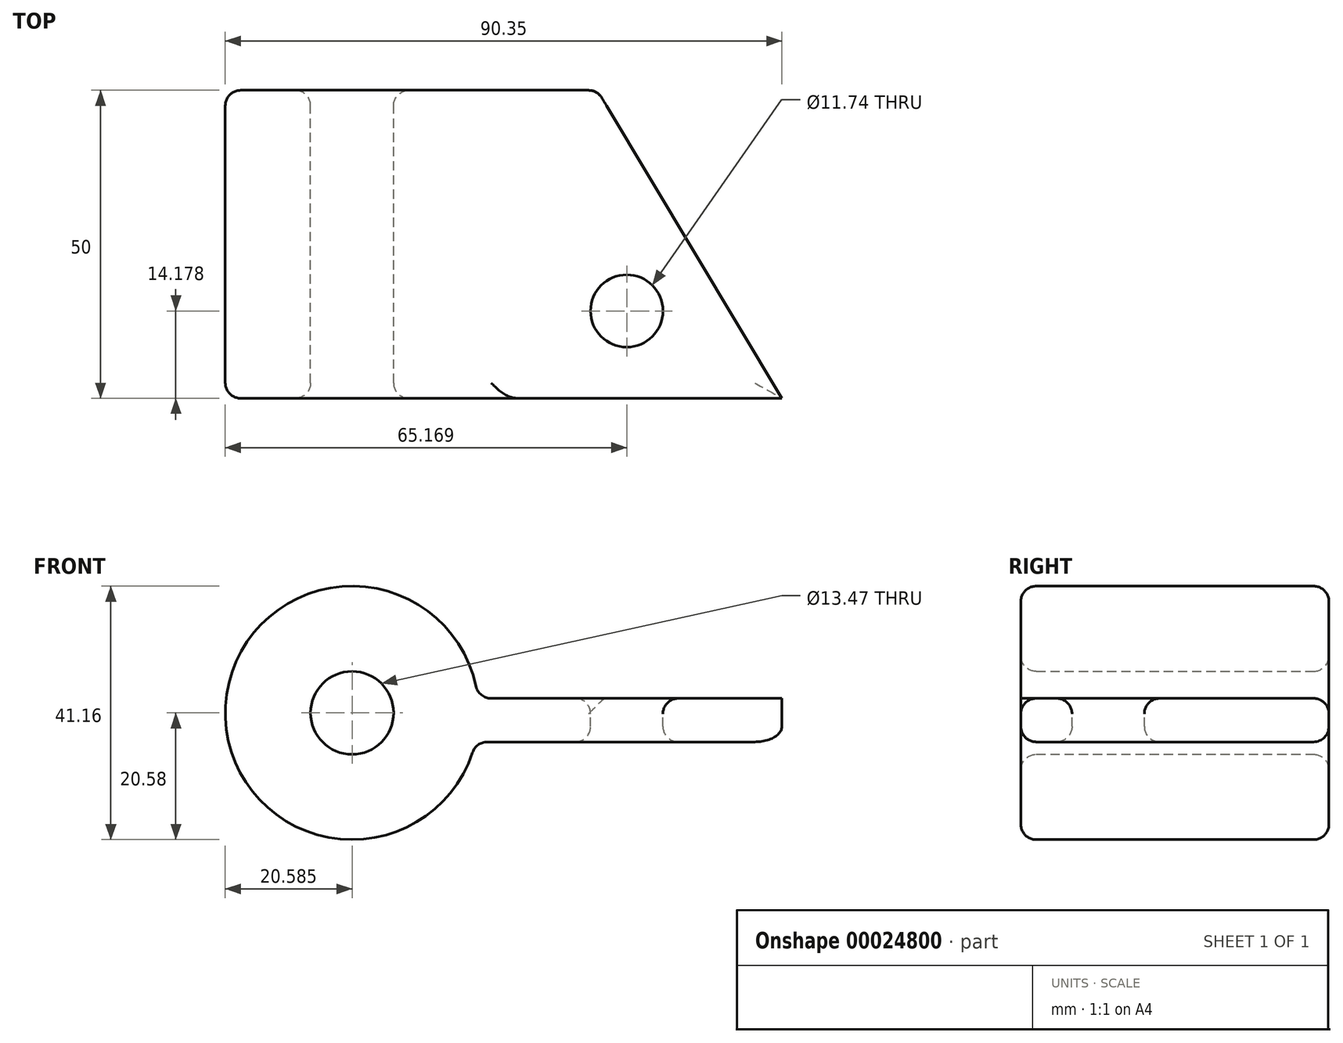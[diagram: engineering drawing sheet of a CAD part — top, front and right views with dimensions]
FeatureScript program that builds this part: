
annotation { "Feature Type Name" : "Feature", "Feature Type Description" : "" }
export const myFeature = defineFeature(function(context is Context, id is Id, definition is map)
    precondition{}
    {
        {
            var Q0;
            Q0=qCreatedBy(makeId("Front.planeOp"),FACE);
            var sketch = newSketch(context, id + "F0", { "sketchPlane" : qUnion([Q0])});
            skCircle(sketch, "E0", {"center": v(-44.76, 6.82) * mm, "radius": 20.58 * mm});
            skCircle(sketch, "E1", {"center": v(-44.76, 6.82) * mm, "radius": 6.74 * mm});
            skSolve(sketch);
        }
        {
            var Q0;
            Q0=makeQuery(id+"F0.imprint","IMPRINT",FACE,{"disambiguationData":[TD([[makeQuery(id+"F0.imprint","IMPRINT",EDGE,{"derivedFrom":sQuery(id+"F0.wireOp",EDGE,"E0")}),1.0]])]});
            extrude(context, id + "F1", {"entities" : qUnion([Q0]), "depth" : 50 * mm});
        }
        {
            var Q0;
            Q0=qCreatedBy(makeId("Right.planeOp"),FACE);
            var sketch = newSketch(context, id + "F2", { "sketchPlane" : qUnion([Q0])});
            skLineSegment(sketch, "E2.bottom", {"start": v(-50.14, 9.18) * mm, "end": v(0, 9.18) * mm});
            skLineSegment(sketch, "E2.top", {"start": v(-50.14, 2.1) * mm, "end": v(0, 2.1) * mm});
            skLineSegment(sketch, "E2.left", {"start": v(-50.14, 9.18) * mm, "end": v(-50.14, 2.1) * mm});
            skLineSegment(sketch, "E2.right", {"start": v(0, 9.18) * mm, "end": v(0, 2.1) * mm});
            skSolve(sketch);
        }
        {
            var Q0;
            Q0=makeQuery(id+"F2.imprint","IMPRINT",FACE,{"disambiguationData":[TD([[makeQuery(id+"F2.imprint","IMPRINT",EDGE,{"derivedFrom":sQuery(id+"F2.wireOp",EDGE,"E2.bottom")}),-1.0]])]});
            extrude(context, id + "F3", {"entities" : qUnion([Q0]), "oppositeDirection" : true, "depth" : 25 * mm});
        }
        {
            var Q0;
            Q0=makeQuery(id+"F3.opExtrude","SWEPT_BODY",BODY,{"disambiguationData":[OSD([sQuery(id+"F2.wireOp",EDGE,"E2.bottom"),sQuery(id+"F2.wireOp",EDGE,"E2.top"),sQuery(id+"F2.wireOp",EDGE,"E2.left"),sQuery(id+"F2.wireOp",EDGE,"E2.right")])]});
            var Q1;
            Q1=makeQuery(id+"F1.opExtrude","SWEPT_BODY",BODY,{"disambiguationData":[OSD([sQuery(id+"F0.wireOp",EDGE,"E0"),sQuery(id+"F0.wireOp",EDGE,"E1")])]});
            booleanBodies(context, id + "F4", {"operationType" : BooleanOperationType.UNION, "tools" : qUnion([Q0, Q1])});
        }
        {
            var Q0;
            Q0=makeQuery(id+"F3.opExtrude","CAP_FACE",FACE,{"disambiguationData":[OSD([sQuery(id+"F2.wireOp",EDGE,"E2.bottom"),sQuery(id+"F2.wireOp",EDGE,"E2.top"),sQuery(id+"F2.wireOp",EDGE,"E2.left"),sQuery(id+"F2.wireOp",EDGE,"E2.right")])],"isStart":true});
            extrude(context, id + "F5", {"entities" : qUnion([Q0]), "operationType" : NewBodyOperationType.ADD, "depth" : 25 * mm});
        }
        {
            var Q0;
            {var subQ0=sQuery(id+"F2.wireOp",EDGE,"E2.left");Q0=makeQuery(id+"F5.boolean.opBoolean","MERGE",FACE,{"derivedFrom":[makeQuery(id+"F3.opExtrude","SWEPT_FACE",FACE,{"disambiguationData":[OSD([subQ0])]}),makeQuery(id+"F5.opExtrude","SWEPT_FACE",FACE,{"disambiguationData":[OSD([subQ0])]})]});}
            var Q1;
            Q1=makeQuery(id+"F1.opExtrude","CAP_FACE",FACE,{"disambiguationData":[OSD([sQuery(id+"F0.wireOp",EDGE,"E0"),sQuery(id+"F0.wireOp",EDGE,"E1")])],"isStart":false});
            extrude(context, id + "F6", {"entities" : qUnion([Q0]), "operationType" : NewBodyOperationType.REMOVE, "endBound" : BoundingType.UP_TO_SURFACE, "oppositeDirection" : true, "endBoundEntityFace" : qUnion([Q1]), "depth" : 25 * mm});
        }
        {
            var Q0;
            {var subQ0=sQuery(id+"F2.wireOp",EDGE,"E2.bottom");Q0=makeQuery(id+"F5.boolean.opBoolean","MERGE",FACE,{"derivedFrom":[makeQuery(id+"F3.opExtrude","SWEPT_FACE",FACE,{"disambiguationData":[OSD([subQ0])]}),makeQuery(id+"F5.opExtrude","SWEPT_FACE",FACE,{"disambiguationData":[OSD([subQ0])]})]});}
            var sketch = newSketch(context, id + "F7", { "sketchPlane" : qUnion([Q0])});
            skLineSegment(sketch, "E3", {"start": v(25, -50) * mm, "end": v(-4.96, 0) * mm});
            skSolve(sketch);
        }
        {
            var Q0;
            {var subQ3=sQuery(id+"F7.wireOp",EDGE,"E3");Q0=makeQuery(id+"F7.imprint","IMPRINT",FACE,{"disambiguationData":[TD([[makeQuery(id+"F7.imprint","IMPRINT",EDGE,{"derivedFrom":subQ3}),-1.0]])]});}
            extrude(context, id + "F8", {"entities" : qUnion([Q0]), "operationType" : NewBodyOperationType.REMOVE, "endBound" : BoundingType.THROUGH_ALL, "oppositeDirection" : true, "depth" : 25 * mm});
        }
        {
            var Q0;
            {var subQ0=sQuery(id+"F2.wireOp",EDGE,"E2.bottom");Q0=makeQuery(id+"F5.boolean.opBoolean","MERGE",FACE,{"derivedFrom":[makeQuery(id+"F3.opExtrude","SWEPT_FACE",FACE,{"disambiguationData":[OSD([subQ0])]}),makeQuery(id+"F5.opExtrude","SWEPT_FACE",FACE,{"disambiguationData":[OSD([subQ0])]})]});}
            var sketch = newSketch(context, id + "F9", { "sketchPlane" : qUnion([Q0])});
            skCircle(sketch, "E4", {"center": v(-0.18, -35.82) * mm, "radius": 5.87 * mm});
            skSolve(sketch);
        }
        {
            var Q0;
            Q0=makeQuery(id+"F9.imprint","IMPRINT",FACE,{"disambiguationData":[TD([[makeQuery(id+"F9.imprint","IMPRINT",EDGE,{"derivedFrom":sQuery(id+"F9.wireOp",EDGE,"E4")}),1.0]])]});
            extrude(context, id + "F10", {"entities" : qUnion([Q0]), "operationType" : NewBodyOperationType.REMOVE, "endBound" : BoundingType.THROUGH_ALL, "oppositeDirection" : true, "depth" : 25 * mm});
        }
        {
            var Q0;
            {var subQ0=sQuery(id+"F2.wireOp",EDGE,"E2.top");Q0=makeQuery(id+"F5.boolean.opBoolean","MERGE",FACE,{"derivedFrom":[makeQuery(id+"F3.opExtrude","SWEPT_FACE",FACE,{"disambiguationData":[OSD([subQ0])]}),makeQuery(id+"F5.opExtrude","SWEPT_FACE",FACE,{"disambiguationData":[OSD([subQ0])]})]});}
            var Q1;
            Q1=makeQuery(id+"F1.opExtrude","SWEPT_FACE",FACE,{"disambiguationData":[OSD([sQuery(id+"F0.wireOp",EDGE,"E0")])]});
            var Q2;
            {var subQ0=sQuery(id+"F2.wireOp",EDGE,"E2.right");Q2=makeQuery(id+"F5.boolean.opBoolean","MERGE",FACE,{"derivedFrom":[makeQuery(id+"F4.opBoolean","MERGE",FACE,{"derivedFrom":[makeQuery(id+"F1.opExtrude","CAP_FACE",FACE,{"disambiguationData":[OSD([sQuery(id+"F0.wireOp",EDGE,"E0"),sQuery(id+"F0.wireOp",EDGE,"E1")])],"isStart":true}),makeQuery(id+"F3.opExtrude","SWEPT_FACE",FACE,{"disambiguationData":[OSD([subQ0])]})]}),makeQuery(id+"F5.opExtrude","SWEPT_FACE",FACE,{"disambiguationData":[OSD([subQ0])]})]});}
            var Q3;
            Q3=makeQuery(id+"F10.boolean.opBoolean","COPY",FACE,{"derivedFrom":makeQuery(id+"F10.opExtrude","SWEPT_FACE",FACE,{"disambiguationData":[OSD([sQuery(id+"F9.wireOp",EDGE,"E4")])]})});
            var Q4;
            Q4=makeQuery(id+"F1.opExtrude","SWEPT_FACE",FACE,{"disambiguationData":[OSD([sQuery(id+"F0.wireOp",EDGE,"E1")])]});
            fillet(context, id + "F11", {"entities" : qUnion([Q0, Q1, Q2, Q3, Q4]), "radius" : 2.5 * mm, "tangentPropagation" : true, "allowEdgeOverflow" : false});
        }
    });
